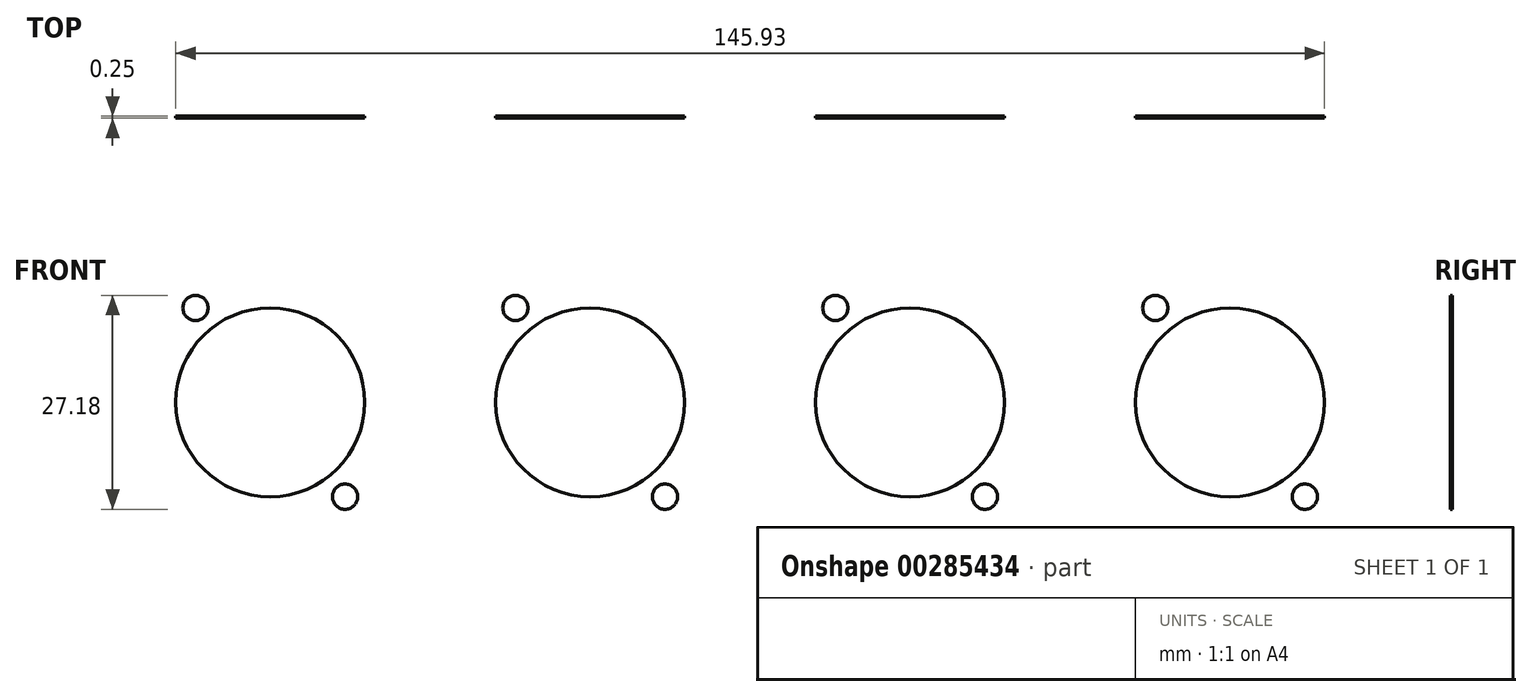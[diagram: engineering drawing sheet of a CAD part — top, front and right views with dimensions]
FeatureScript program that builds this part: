
annotation { "Feature Type Name" : "Feature", "Feature Type Description" : "" }
export const myFeature = defineFeature(function(context is Context, id is Id, definition is map)
    precondition{}
    {
        {
            var Q0;
            Q0=qCreatedBy(makeId("Front.planeOp"),FACE);
            var sketch = newSketch(context, id + "F0", { "sketchPlane" : qUnion([Q0])});
            skLineSegment(sketch, "E0.bottom", {"start": v(125.42, 19.56) * mm, "end": v(152.7, 19.56) * mm, "construction": true});
            skLineSegment(sketch, "E0.top", {"start": v(125.42, -19.56) * mm, "end": v(152.7, -19.56) * mm, "construction": true});
            skLineSegment(sketch, "E0.left", {"start": v(121.92, 16.06) * mm, "end": v(121.92, -16.06) * mm, "construction": true});
            skLineSegment(sketch, "E0.right", {"start": v(156.21, 16.06) * mm, "end": v(156.21, -16.06) * mm, "construction": true});
            skPoint(sketch, "E1.visualSharp", {"position": v(121.92, 19.56) * mm});
            skArc(sketch, "E1.filletArc", {"start": v(125.42, 19.56) * mm, "mid": v(122.95, 18.53) * mm, "end": v(121.92, 16.06) * mm, "construction": true});
            skPoint(sketch, "E2.visualSharp", {"position": v(156.21, 19.56) * mm});
            skArc(sketch, "E2.filletArc", {"start": v(156.21, 16.06) * mm, "mid": v(155.18, 18.53) * mm, "end": v(152.7, 19.56) * mm, "construction": true});
            skPoint(sketch, "E3.visualSharp", {"position": v(121.92, -19.56) * mm});
            skArc(sketch, "E3.filletArc", {"start": v(121.92, -16.06) * mm, "mid": v(122.95, -18.53) * mm, "end": v(125.42, -19.56) * mm, "construction": true});
            skPoint(sketch, "E4.visualSharp", {"position": v(156.21, -19.56) * mm});
            skArc(sketch, "E4.filletArc", {"start": v(152.7, -19.56) * mm, "mid": v(155.18, -18.53) * mm, "end": v(156.21, -16.06) * mm, "construction": true});
            skLineSegment(sketch, "E5.bottom", {"start": v(84.78, 19.56) * mm, "end": v(112.07, 19.56) * mm, "construction": true});
            skLineSegment(sketch, "E5.top", {"start": v(84.78, -19.56) * mm, "end": v(112.07, -19.56) * mm, "construction": true});
            skLineSegment(sketch, "E5.left", {"start": v(81.28, 16.06) * mm, "end": v(81.28, -16.06) * mm, "construction": true});
            skLineSegment(sketch, "E5.right", {"start": v(115.57, 16.06) * mm, "end": v(115.57, -16.06) * mm, "construction": true});
            skPoint(sketch, "E6.visualSharp", {"position": v(81.28, 19.56) * mm});
            skArc(sketch, "E6.filletArc", {"start": v(84.78, 19.56) * mm, "mid": v(82.3, 18.53) * mm, "end": v(81.28, 16.06) * mm, "construction": true});
            skPoint(sketch, "E7.visualSharp", {"position": v(115.57, 19.56) * mm});
            skArc(sketch, "E7.filletArc", {"start": v(115.57, 16.06) * mm, "mid": v(114.54, 18.53) * mm, "end": v(112.07, 19.56) * mm, "construction": true});
            skPoint(sketch, "E8.visualSharp", {"position": v(81.28, -19.56) * mm});
            skArc(sketch, "E8.filletArc", {"start": v(81.28, -16.06) * mm, "mid": v(82.3, -18.53) * mm, "end": v(84.78, -19.56) * mm, "construction": true});
            skPoint(sketch, "E9.visualSharp", {"position": v(115.57, -19.56) * mm});
            skArc(sketch, "E9.filletArc", {"start": v(112.07, -19.56) * mm, "mid": v(114.54, -18.53) * mm, "end": v(115.57, -16.06) * mm, "construction": true});
            skLineSegment(sketch, "E10.bottom", {"start": v(44.14, 19.56) * mm, "end": v(71.43, 19.56) * mm, "construction": true});
            skLineSegment(sketch, "E10.top", {"start": v(44.14, -19.56) * mm, "end": v(71.43, -19.56) * mm, "construction": true});
            skLineSegment(sketch, "E10.left", {"start": v(40.64, 16.06) * mm, "end": v(40.64, -16.06) * mm, "construction": true});
            skLineSegment(sketch, "E10.right", {"start": v(74.93, 16.06) * mm, "end": v(74.93, -16.06) * mm, "construction": true});
            skPoint(sketch, "E11.visualSharp", {"position": v(40.64, 19.56) * mm});
            skArc(sketch, "E11.filletArc", {"start": v(44.14, 19.56) * mm, "mid": v(41.67, 18.53) * mm, "end": v(40.64, 16.06) * mm, "construction": true});
            skPoint(sketch, "E12.visualSharp", {"position": v(74.93, 19.56) * mm});
            skArc(sketch, "E12.filletArc", {"start": v(74.93, 16.06) * mm, "mid": v(73.9, 18.53) * mm, "end": v(71.43, 19.56) * mm, "construction": true});
            skPoint(sketch, "E13.visualSharp", {"position": v(40.64, -19.56) * mm});
            skArc(sketch, "E13.filletArc", {"start": v(40.64, -16.06) * mm, "mid": v(41.67, -18.53) * mm, "end": v(44.14, -19.56) * mm, "construction": true});
            skPoint(sketch, "E14.visualSharp", {"position": v(74.93, -19.56) * mm});
            skArc(sketch, "E14.filletArc", {"start": v(71.43, -19.56) * mm, "mid": v(73.9, -18.53) * mm, "end": v(74.93, -16.06) * mm, "construction": true});
            skLineSegment(sketch, "E15.bottom", {"start": v(3.5, 19.56) * mm, "end": v(30.79, 19.56) * mm, "construction": true});
            skLineSegment(sketch, "E15.top", {"start": v(3.5, -19.56) * mm, "end": v(30.79, -19.56) * mm, "construction": true});
            skLineSegment(sketch, "E15.left", {"start": v(0, 16.06) * mm, "end": v(0, -16.06) * mm, "construction": true});
            skLineSegment(sketch, "E15.right", {"start": v(34.3, 16.06) * mm, "end": v(34.3, -16.06) * mm, "construction": true});
            skPoint(sketch, "E16.visualSharp", {"position": v(0, 19.56) * mm});
            skArc(sketch, "E16.filletArc", {"start": v(3.5, 19.56) * mm, "mid": v(1.03, 18.53) * mm, "end": v(0, 16.06) * mm, "construction": true});
            skPoint(sketch, "E17.visualSharp", {"position": v(34.29, 19.56) * mm});
            skArc(sketch, "E17.filletArc", {"start": v(34.3, 16.06) * mm, "mid": v(33.26, 18.53) * mm, "end": v(30.79, 19.56) * mm, "construction": true});
            skPoint(sketch, "E18.visualSharp", {"position": v(0, -19.56) * mm});
            skArc(sketch, "E18.filletArc", {"start": v(0, -16.06) * mm, "mid": v(1.03, -18.53) * mm, "end": v(3.5, -19.56) * mm, "construction": true});
            skPoint(sketch, "E19.visualSharp", {"position": v(34.29, -19.56) * mm});
            skArc(sketch, "E19.filletArc", {"start": v(30.79, -19.56) * mm, "mid": v(33.26, -18.53) * mm, "end": v(34.3, -16.06) * mm, "construction": true});
            skLineSegment(sketch, "E20", {"start": v(0, 0) * mm, "end": v(156.21, 0) * mm, "construction": true});
            skPoint(sketch, "E21", {"position": v(0, 0) * mm});
            skLineSegment(sketch, "E22", {"start": v(17.15, 19.56) * mm, "end": v(17.15, -19.56) * mm, "construction": true});
            skLineSegment(sketch, "E23", {"start": v(57.79, 19.56) * mm, "end": v(57.79, -19.56) * mm, "construction": true});
            skLineSegment(sketch, "E24", {"start": v(98.43, 19.56) * mm, "end": v(98.43, -19.56) * mm, "construction": true});
            skLineSegment(sketch, "E25", {"start": v(139.07, 19.56) * mm, "end": v(139.07, -19.56) * mm, "construction": true});
            skCircle(sketch, "E26", {"center": v(17.15, 0) * mm, "radius": 12 * mm});
            skCircle(sketch, "E27", {"center": v(57.79, 0) * mm, "radius": 12 * mm});
            skCircle(sketch, "E28", {"center": v(98.43, 0) * mm, "radius": 12 * mm});
            skCircle(sketch, "E29", {"center": v(139.07, 0) * mm, "radius": 12 * mm});
            skCircle(sketch, "E30", {"center": v(7.65, 11.99) * mm, "radius": 1.6 * mm});
            skCircle(sketch, "E31", {"center": v(26.64, -11.99) * mm, "radius": 1.6 * mm});
            skCircle(sketch, "E32", {"center": v(48.29, 11.99) * mm, "radius": 1.6 * mm});
            skCircle(sketch, "E33", {"center": v(67.28, -11.99) * mm, "radius": 1.6 * mm});
            skCircle(sketch, "E34", {"center": v(88.93, 11.99) * mm, "radius": 1.6 * mm});
            skCircle(sketch, "E35", {"center": v(107.92, -11.99) * mm, "radius": 1.6 * mm});
            skCircle(sketch, "E36", {"center": v(129.57, 11.99) * mm, "radius": 1.6 * mm});
            skCircle(sketch, "E37", {"center": v(148.56, -11.99) * mm, "radius": 1.6 * mm});
            skLineSegment(sketch, "E38.bottom", {"start": v(7.52, 15.5) * mm, "end": v(26.77, 15.5) * mm, "construction": true});
            skLineSegment(sketch, "E38.top", {"start": v(7.52, -15.5) * mm, "end": v(26.77, -15.5) * mm, "construction": true});
            skLineSegment(sketch, "E38.left", {"start": v(4.34, 12.32) * mm, "end": v(4.34, -12.32) * mm, "construction": true});
            skLineSegment(sketch, "E38.right", {"start": v(29.95, 12.32) * mm, "end": v(29.95, -12.32) * mm, "construction": true});
            skPoint(sketch, "E39.visualSharp", {"position": v(4.34, 15.5) * mm});
            skArc(sketch, "E39.filletArc", {"start": v(7.52, 15.5) * mm, "mid": v(5.27, 14.56) * mm, "end": v(4.34, 12.32) * mm, "construction": true});
            skPoint(sketch, "E40.visualSharp", {"position": v(29.95, 15.5) * mm});
            skArc(sketch, "E40.filletArc", {"start": v(29.95, 12.32) * mm, "mid": v(29.02, 14.56) * mm, "end": v(26.77, 15.5) * mm, "construction": true});
            skPoint(sketch, "E41.visualSharp", {"position": v(29.95, -15.5) * mm});
            skArc(sketch, "E41.filletArc", {"start": v(26.77, -15.5) * mm, "mid": v(29.02, -14.56) * mm, "end": v(29.95, -12.32) * mm, "construction": true});
            skPoint(sketch, "E42.visualSharp", {"position": v(4.34, -15.5) * mm});
            skArc(sketch, "E42.filletArc", {"start": v(4.34, -12.32) * mm, "mid": v(5.27, -14.56) * mm, "end": v(7.52, -15.5) * mm, "construction": true});
            skSolve(sketch);
        }
        {
            var Q0;
            Q0=makeQuery(id+"F0.imprint","IMPRINT",FACE,{"disambiguationData":[TD([[makeQuery(id+"F0.imprint","IMPRINT",EDGE,{"derivedFrom":sQuery(id+"F0.wireOp",EDGE,"E26")}),1.0]])]});
            var Q1;
            Q1=makeQuery(id+"F0.imprint","IMPRINT",FACE,{"disambiguationData":[TD([[makeQuery(id+"F0.imprint","IMPRINT",EDGE,{"derivedFrom":sQuery(id+"F0.wireOp",EDGE,"E30")}),1.0]])]});
            var Q2;
            Q2=makeQuery(id+"F0.imprint","IMPRINT",FACE,{"disambiguationData":[TD([[makeQuery(id+"F0.imprint","IMPRINT",EDGE,{"derivedFrom":sQuery(id+"F0.wireOp",EDGE,"E31")}),1.0]])]});
            var Q3;
            Q3=makeQuery(id+"F0.imprint","IMPRINT",FACE,{"disambiguationData":[TD([[makeQuery(id+"F0.imprint","IMPRINT",EDGE,{"derivedFrom":sQuery(id+"F0.wireOp",EDGE,"E27")}),1.0]])]});
            var Q4;
            Q4=makeQuery(id+"F0.imprint","IMPRINT",FACE,{"disambiguationData":[TD([[makeQuery(id+"F0.imprint","IMPRINT",EDGE,{"derivedFrom":sQuery(id+"F0.wireOp",EDGE,"E32")}),1.0]])]});
            var Q5;
            Q5=makeQuery(id+"F0.imprint","IMPRINT",FACE,{"disambiguationData":[TD([[makeQuery(id+"F0.imprint","IMPRINT",EDGE,{"derivedFrom":sQuery(id+"F0.wireOp",EDGE,"E33")}),1.0]])]});
            var Q6;
            Q6=makeQuery(id+"F0.imprint","IMPRINT",FACE,{"disambiguationData":[TD([[makeQuery(id+"F0.imprint","IMPRINT",EDGE,{"derivedFrom":sQuery(id+"F0.wireOp",EDGE,"E28")}),1.0]])]});
            var Q7;
            Q7=makeQuery(id+"F0.imprint","IMPRINT",FACE,{"disambiguationData":[TD([[makeQuery(id+"F0.imprint","IMPRINT",EDGE,{"derivedFrom":sQuery(id+"F0.wireOp",EDGE,"E34")}),1.0]])]});
            var Q8;
            Q8=makeQuery(id+"F0.imprint","IMPRINT",FACE,{"disambiguationData":[TD([[makeQuery(id+"F0.imprint","IMPRINT",EDGE,{"derivedFrom":sQuery(id+"F0.wireOp",EDGE,"E35")}),1.0]])]});
            var Q9;
            Q9=makeQuery(id+"F0.imprint","IMPRINT",FACE,{"disambiguationData":[TD([[makeQuery(id+"F0.imprint","IMPRINT",EDGE,{"derivedFrom":sQuery(id+"F0.wireOp",EDGE,"E29")}),1.0]])]});
            var Q10;
            Q10=makeQuery(id+"F0.imprint","IMPRINT",FACE,{"disambiguationData":[TD([[makeQuery(id+"F0.imprint","IMPRINT",EDGE,{"derivedFrom":sQuery(id+"F0.wireOp",EDGE,"E36")}),1.0]])]});
            var Q11;
            Q11=makeQuery(id+"F0.imprint","IMPRINT",FACE,{"disambiguationData":[TD([[makeQuery(id+"F0.imprint","IMPRINT",EDGE,{"derivedFrom":sQuery(id+"F0.wireOp",EDGE,"E37")}),1.0]])]});
            extrude(context, id + "F1", {"entities" : qUnion([Q0, Q1, Q2, Q3, Q4, Q5, Q6, Q7, Q8, Q9, Q10, Q11]), "depth" : 0.25 * mm});
        }
    });
